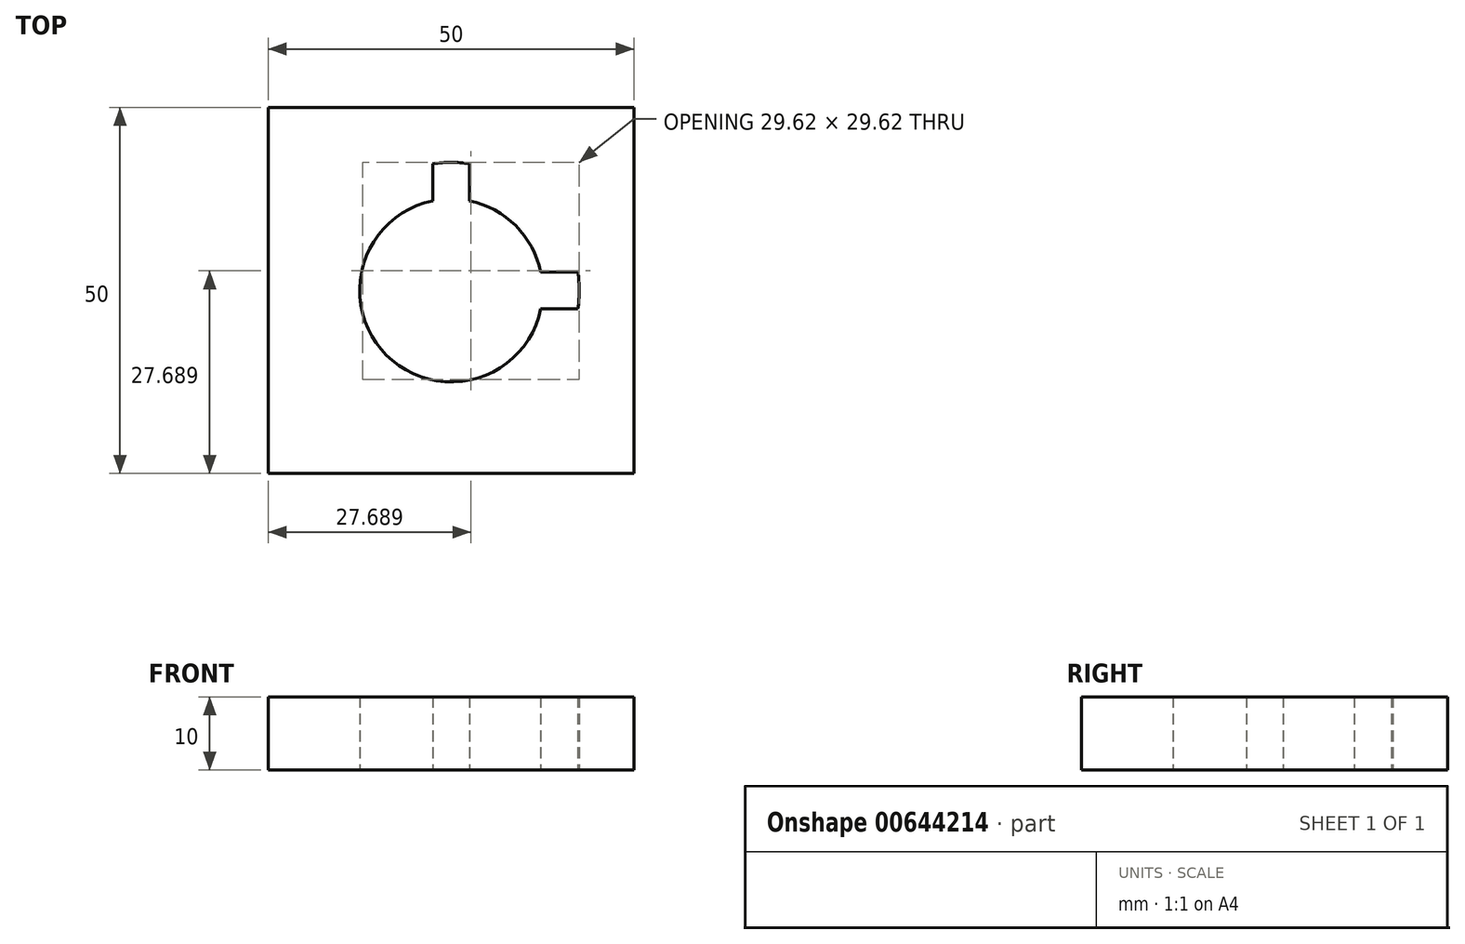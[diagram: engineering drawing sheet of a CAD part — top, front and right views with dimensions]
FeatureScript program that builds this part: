
annotation { "Feature Type Name" : "Feature", "Feature Type Description" : "" }
export const myFeature = defineFeature(function(context is Context, id is Id, definition is map)
    precondition{}
    {
        {
            var Q0;
            Q0=qCreatedBy(makeId("Top.planeOp"),FACE);
            var sketch = newSketch(context, id + "F0", { "sketchPlane" : qUnion([Q0])});
            skLineSegment(sketch, "E0.bottom", {"start": v(25, -25) * mm, "end": v(-25, -25) * mm});
            skLineSegment(sketch, "E0.top", {"start": v(25, 25) * mm, "end": v(-25, 25) * mm});
            skLineSegment(sketch, "E0.left", {"start": v(25, -25) * mm, "end": v(25, 25) * mm});
            skLineSegment(sketch, "E0.right", {"start": v(-25, -25) * mm, "end": v(-25, 25) * mm});
            skPoint(sketch, "E0.middle", {"position": v(0, 0) * mm});
            skCircle(sketch, "E1", {"center": v(0, 0) * mm, "radius": 12.5 * mm});
            skLineSegment(sketch, "E2.bottom", {"start": v(2.5, -18.6) * mm, "end": v(-2.5, -18.6) * mm});
            skLineSegment(sketch, "E2.top", {"start": v(2.5, 18.6) * mm, "end": v(-2.5, 18.6) * mm});
            skLineSegment(sketch, "E2.left", {"start": v(2.5, -18.6) * mm, "end": v(2.5, 18.6) * mm});
            skLineSegment(sketch, "E2.right", {"start": v(-2.5, -18.6) * mm, "end": v(-2.5, 18.6) * mm});
            skLineSegment(sketch, "E3.bottom", {"start": v(21.12, -2.5) * mm, "end": v(-21.12, -2.5) * mm});
            skLineSegment(sketch, "E3.top", {"start": v(21.12, 2.5) * mm, "end": v(-21.12, 2.5) * mm});
            skLineSegment(sketch, "E3.left", {"start": v(21.12, -2.5) * mm, "end": v(21.12, 2.5) * mm});
            skLineSegment(sketch, "E3.right", {"start": v(-21.12, -2.5) * mm, "end": v(-21.12, 2.5) * mm});
            skCircle(sketch, "E4", {"center": v(0, 0) * mm, "radius": 17.5 * mm});
            skSolve(sketch);
        }
        {
            var Q0;
            Q0=makeQuery(id+"F0.imprint","IMPRINT",FACE,{"disambiguationData":[TD([[makeQuery(id+"F0.imprint","IMPRINT",EDGE,{"derivedFrom":sQuery(id+"F0.wireOp",EDGE,"E0.bottom")}),-1.0]])]});
            var Q1;
            {var subQ0=sQuery(id+"F0.wireOp",EDGE,"E2.top");Q1=makeQuery(id+"F0.imprint","IMPRINT",FACE,{"disambiguationData":[TD([[makeQuery(id+"F0.imprint","IMPRINT",EDGE,{"derivedFrom":subQ0}),1.0]])]});}
            var Q2;
            {var subQ0=sQuery(id+"F0.wireOp",EDGE,"E3.right");Q2=makeQuery(id+"F0.imprint","IMPRINT",FACE,{"disambiguationData":[TD([[makeQuery(id+"F0.imprint","IMPRINT",EDGE,{"derivedFrom":subQ0}),-1.0]])]});}
            var Q3;
            {var subQ0=sQuery(id+"F0.wireOp",EDGE,"E2.bottom");Q3=makeQuery(id+"F0.imprint","IMPRINT",FACE,{"disambiguationData":[TD([[makeQuery(id+"F0.imprint","IMPRINT",EDGE,{"derivedFrom":subQ0}),-1.0]])]});}
            var Q4;
            {var subQ0=sQuery(id+"F0.wireOp",EDGE,"E3.left");Q4=makeQuery(id+"F0.imprint","IMPRINT",FACE,{"disambiguationData":[TD([[makeQuery(id+"F0.imprint","IMPRINT",EDGE,{"derivedFrom":subQ0}),1.0]])]});}
            var Q5;
            {var subQ0=sQuery(id+"F0.wireOp",EDGE,"E2.left");var subQ1=sQuery(id+"F0.wireOp",EDGE,"E1");var subQ2=makeQuery(id+"F0.imprint","INTERSECT",VERTEX,{"disambiguationData":[OD(0.0)],"derivedFrom":[subQ1,subQ0]});Q5=makeQuery(id+"F0.imprint","IMPRINT",FACE,{"disambiguationData":[TD([[makeQuery(id+"F0.imprint","IMPRINT",EDGE,{"disambiguationData":[TD([[subQ2,1.0]])],"derivedFrom":subQ1}),-1.0]])]});}
            var Q6;
            {var subQ0=sQuery(id+"F0.wireOp",EDGE,"E2.left");var subQ1=sQuery(id+"F0.wireOp",EDGE,"E1");var subQ2=makeQuery(id+"F0.imprint","INTERSECT",VERTEX,{"disambiguationData":[OD(1.0)],"derivedFrom":[subQ1,subQ0]});Q6=makeQuery(id+"F0.imprint","IMPRINT",FACE,{"disambiguationData":[TD([[makeQuery(id+"F0.imprint","IMPRINT",EDGE,{"disambiguationData":[TD([[subQ2,-1.0]])],"derivedFrom":subQ1}),-1.0]])]});}
            var Q7;
            {var subQ0=sQuery(id+"F0.wireOp",EDGE,"E2.right");var subQ1=sQuery(id+"F0.wireOp",EDGE,"E1");var subQ2=makeQuery(id+"F0.imprint","INTERSECT",VERTEX,{"disambiguationData":[OD(1.0)],"derivedFrom":[subQ1,subQ0]});Q7=makeQuery(id+"F0.imprint","IMPRINT",FACE,{"disambiguationData":[TD([[makeQuery(id+"F0.imprint","IMPRINT",EDGE,{"disambiguationData":[TD([[subQ2,-1.0]])],"derivedFrom":subQ1}),-1.0]])]});}
            var Q8;
            {var subQ0=sQuery(id+"F0.wireOp",EDGE,"E3.bottom");var subQ1=sQuery(id+"F0.wireOp",EDGE,"E1");var subQ2=makeQuery(id+"F0.imprint","INTERSECT",VERTEX,{"disambiguationData":[OD(0.0)],"derivedFrom":[subQ1,subQ0]});Q8=makeQuery(id+"F0.imprint","IMPRINT",FACE,{"disambiguationData":[TD([[makeQuery(id+"F0.imprint","IMPRINT",EDGE,{"disambiguationData":[TD([[subQ2,-1.0]])],"derivedFrom":subQ1}),-1.0]])]});}
            var Q9;
            {var subQ0=sQuery(id+"F0.wireOp",EDGE,"E3.top");var subQ1=sQuery(id+"F0.wireOp",EDGE,"E1");var subQ2=makeQuery(id+"F0.imprint","INTERSECT",VERTEX,{"disambiguationData":[OD(1.0)],"derivedFrom":[subQ1,subQ0]});Q9=makeQuery(id+"F0.imprint","IMPRINT",FACE,{"disambiguationData":[TD([[makeQuery(id+"F0.imprint","IMPRINT",EDGE,{"disambiguationData":[TD([[subQ2,-1.0]])],"derivedFrom":subQ1}),-1.0]])]});}
            var Q10;
            {var subQ0=sQuery(id+"F0.wireOp",EDGE,"E2.right");var subQ1=sQuery(id+"F0.wireOp",EDGE,"E1");var subQ2=makeQuery(id+"F0.imprint","INTERSECT",VERTEX,{"disambiguationData":[OD(0.0)],"derivedFrom":[subQ1,subQ0]});Q10=makeQuery(id+"F0.imprint","IMPRINT",FACE,{"disambiguationData":[TD([[makeQuery(id+"F0.imprint","IMPRINT",EDGE,{"disambiguationData":[TD([[subQ2,-1.0]])],"derivedFrom":subQ1}),-1.0]])]});}
            extrude(context, id + "F1", {"entities" : qUnion([Q0, Q1, Q2, Q3, Q4, Q5, Q6, Q7, Q8, Q9, Q10]), "depth" : 10 * mm, "offsetDistance" : 25 * mm});
        }
    });
